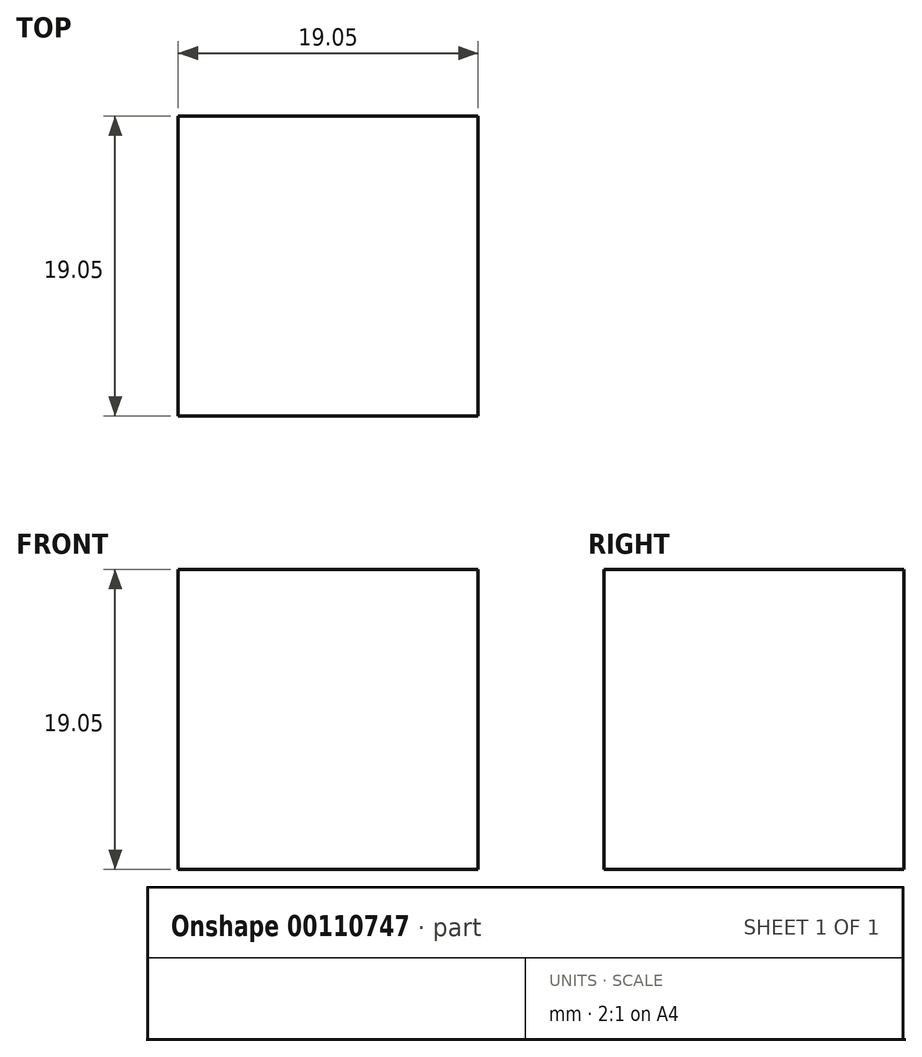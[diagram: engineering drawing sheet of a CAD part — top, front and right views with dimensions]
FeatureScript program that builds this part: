
annotation { "Feature Type Name" : "Feature", "Feature Type Description" : "" }
export const myFeature = defineFeature(function(context is Context, id is Id, definition is map)
    precondition{}
    {
        {
            var Q0;
            Q0=qCreatedBy(makeId("Front.planeOp"),FACE);
            var sketch = newSketch(context, id + "F0", { "sketchPlane" : qUnion([Q0])});
            skLineSegment(sketch, "E0.bottom", {"start": v(0, 0) * mm, "end": v(19.05, 0) * mm});
            skLineSegment(sketch, "E0.top", {"start": v(0, 19.05) * mm, "end": v(19.05, 19.05) * mm});
            skLineSegment(sketch, "E0.left", {"start": v(0, 0) * mm, "end": v(0, 19.05) * mm});
            skLineSegment(sketch, "E0.right", {"start": v(19.05, 0) * mm, "end": v(19.05, 19.05) * mm});
            skSolve(sketch);
        }
        {
            var Q0;
            Q0 = qSketchRegion(id + "F0", true);
            extrude(context, id + "F1", {"entities" : qUnion([Q0]), "depth" : 19.05 * mm});
        }
    });
